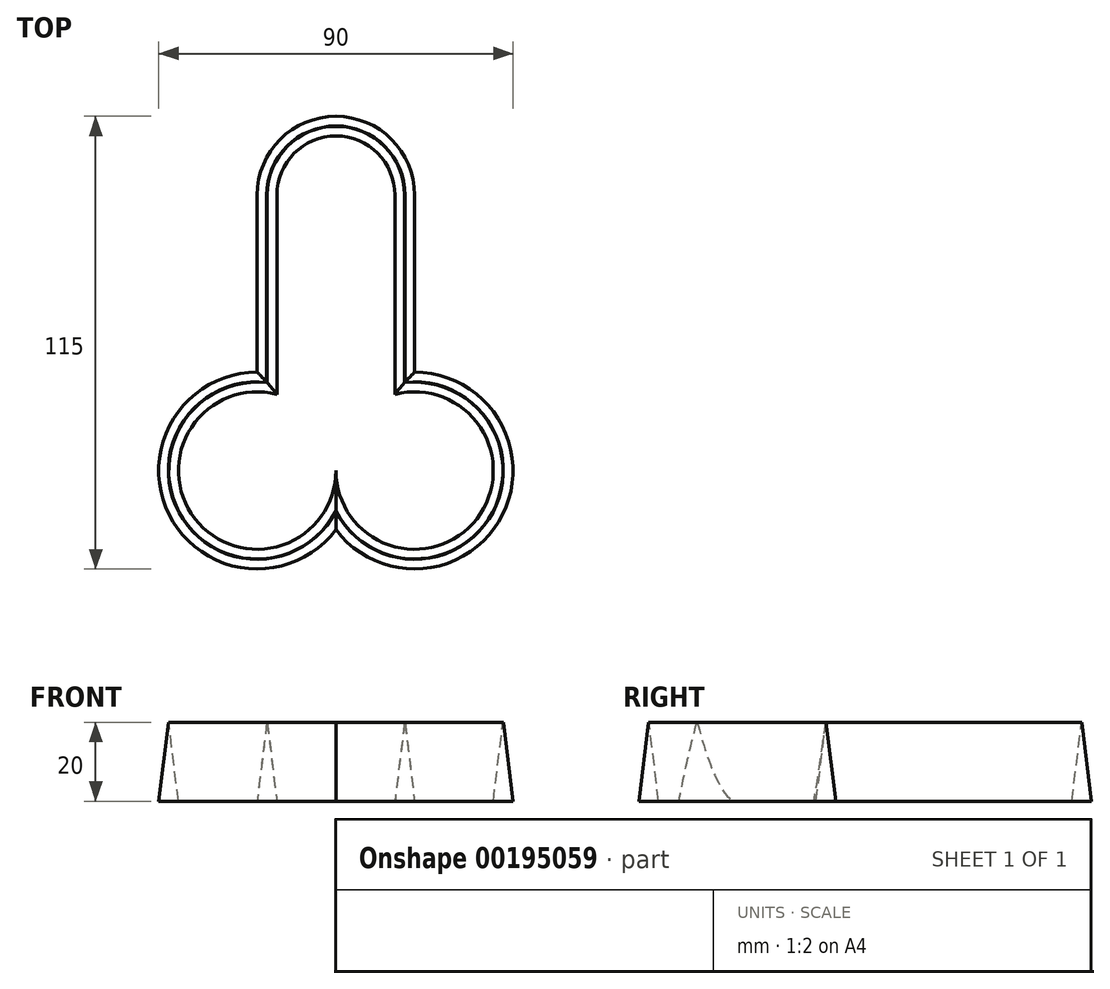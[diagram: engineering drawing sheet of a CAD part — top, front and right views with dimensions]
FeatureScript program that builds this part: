
annotation { "Feature Type Name" : "Feature", "Feature Type Description" : "" }
export const myFeature = defineFeature(function(context is Context, id is Id, definition is map)
    precondition{}
    {
        {
            var Q0;
            Q0=qCreatedBy(makeId("Top.planeOp"),FACE);
            var sketch = newSketch(context, id + "F0", { "sketchPlane" : qUnion([Q0])});
            skArc(sketch, "E0", {"start": v(15, 70) * mm, "mid": v(0, 85) * mm, "end": v(-15, 70) * mm});
            skArc(sketch, "E1", {"start": v(-15, 19.36) * mm, "mid": v(-35.81, -12.25) * mm, "end": v(0, 0) * mm});
            skArc(sketch, "E2", {"start": v(0, 0) * mm, "mid": v(35.81, -12.25) * mm, "end": v(15, 19.36) * mm});
            skLineSegment(sketch, "E3", {"start": v(-15, 70) * mm, "end": v(-15, 19.36) * mm});
            skLineSegment(sketch, "E4", {"start": v(15, 70) * mm, "end": v(15, 19.36) * mm});
            skArc(sketch, "E5.0", {"start": v(-20, 25) * mm, "mid": v(-42.36, -11.18) * mm, "end": v(0, -15) * mm});
            skLineSegment(sketch, "E5.1", {"start": v(-20, 70) * mm, "end": v(-20, 25) * mm});
            skArc(sketch, "E5.2", {"start": v(0, -15) * mm, "mid": v(42.36, -11.18) * mm, "end": v(20, 25) * mm});
            skLineSegment(sketch, "E5.3", {"start": v(20, 70) * mm, "end": v(20, 25) * mm});
            skArc(sketch, "E5.4", {"start": v(20, 70) * mm, "mid": v(0, 90) * mm, "end": v(-20, 70) * mm});
            skSolve(sketch);
        }
        {
            var Q0;
            Q0 = qSketchRegion(id + "F0", true);
            extrude(context, id + "F1", {"entities" : qUnion([Q0]), "depth" : 20 * mm, "hasDraft" : true, "draftAngle" : 7 * degree, "draftPullDirection" : true});
        }
    });
